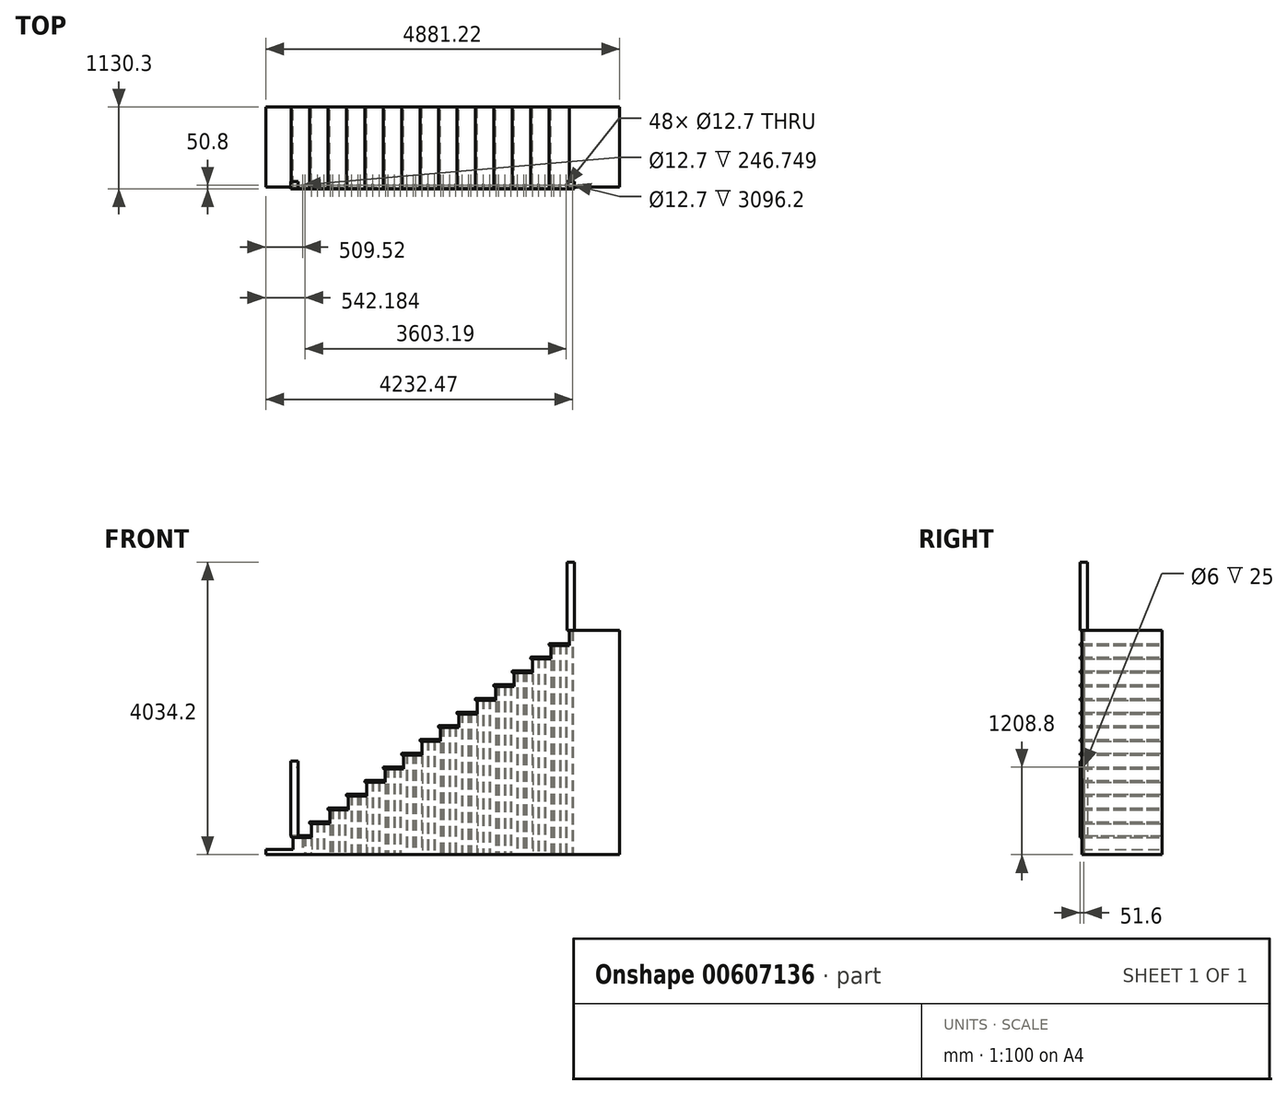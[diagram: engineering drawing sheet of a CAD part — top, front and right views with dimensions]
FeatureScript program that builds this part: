
annotation { "Feature Type Name" : "Feature", "Feature Type Description" : "" }
export const myFeature = defineFeature(function(context is Context, id is Id, definition is map)
    precondition{}
    {
        {
            var Q0;
            Q0=qCreatedBy(makeId("Front.planeOp"),FACE);
            var sketch = newSketch(context, id + "F0", { "sketchPlane" : qUnion([Q0])});
            skLineSegment(sketch, "E0.bottom", {"start": v(9.53, 0) * mm, "end": v(279.4, 0) * mm});
            skLineSegment(sketch, "E0.top", {"start": v(9.53, 25.4) * mm, "end": v(279.4, 25.4) * mm});
            skLineSegment(sketch, "E0.left", {"start": v(0, 9.52) * mm, "end": v(0, 15.88) * mm});
            skLineSegment(sketch, "E0.right", {"start": v(279.4, 0) * mm, "end": v(279.4, 25.4) * mm});
            skPoint(sketch, "E1.visualSharp", {"position": v(0, 25.4) * mm});
            skArc(sketch, "E1.filletArc", {"start": v(9.53, 25.4) * mm, "mid": v(2.79, 22.61) * mm, "end": v(0, 15.87) * mm});
            skPoint(sketch, "E2.visualSharp", {"position": v(0, 0) * mm});
            skArc(sketch, "E2.filletArc", {"start": v(0, 9.52) * mm, "mid": v(2.79, 2.79) * mm, "end": v(9.53, 0) * mm});
            skLineSegment(sketch, "E3.1.0.0", {"start": v(263.53, 189.1) * mm, "end": v(533.4, 189.1) * mm});
            skLineSegment(sketch, "E3.1.0.1", {"start": v(263.53, 214.5) * mm, "end": v(533.4, 214.5) * mm});
            skLineSegment(sketch, "E3.1.0.2", {"start": v(533.4, 189.1) * mm, "end": v(533.4, 214.5) * mm});
            skArc(sketch, "E3.1.0.3", {"start": v(263.53, 214.5) * mm, "mid": v(256.79, 211.71) * mm, "end": v(254, 204.98) * mm});
            skLineSegment(sketch, "E3.1.0.4", {"start": v(254, 198.63) * mm, "end": v(254, 204.98) * mm});
            skArc(sketch, "E3.1.0.5", {"start": v(254, 198.63) * mm, "mid": v(256.79, 191.89) * mm, "end": v(263.53, 189.1) * mm});
            skLineSegment(sketch, "E3.2.0.0", {"start": v(517.52, 378.2) * mm, "end": v(787.4, 378.2) * mm});
            skLineSegment(sketch, "E3.2.0.1", {"start": v(517.52, 403.6) * mm, "end": v(787.4, 403.6) * mm});
            skLineSegment(sketch, "E3.2.0.2", {"start": v(787.4, 378.2) * mm, "end": v(787.4, 403.6) * mm});
            skArc(sketch, "E3.2.0.3", {"start": v(517.52, 403.6) * mm, "mid": v(510.79, 400.81) * mm, "end": v(508, 394.07) * mm});
            skLineSegment(sketch, "E3.2.0.4", {"start": v(508, 387.73) * mm, "end": v(508, 394.07) * mm});
            skArc(sketch, "E3.2.0.5", {"start": v(508, 387.73) * mm, "mid": v(510.79, 380.99) * mm, "end": v(517.52, 378.2) * mm});
            skLineSegment(sketch, "E3.direction1", {"start": v(9.53, 0) * mm, "end": v(263.53, 189.1) * mm, "construction": true});
            skLineSegment(sketch, "E4.0.3.0", {"start": v(771.52, 567.3) * mm, "end": v(1041.4, 567.3) * mm});
            skLineSegment(sketch, "E4.3.3.0", {"start": v(771.52, 592.7) * mm, "end": v(1041.4, 592.7) * mm});
            skLineSegment(sketch, "E4.6.3.0", {"start": v(1041.4, 567.3) * mm, "end": v(1041.4, 592.7) * mm});
            skArc(sketch, "E4.9.3.0", {"start": v(771.52, 592.7) * mm, "mid": v(764.79, 589.91) * mm, "end": v(762, 583.18) * mm});
            skLineSegment(sketch, "E4.13.3.0", {"start": v(762, 576.82) * mm, "end": v(762, 583.18) * mm});
            skArc(sketch, "E4.16.3.0", {"start": v(762, 576.82) * mm, "mid": v(764.79, 570.09) * mm, "end": v(771.52, 567.3) * mm});
            skLineSegment(sketch, "E4.0.4.0", {"start": v(1025.53, 756.4) * mm, "end": v(1295.4, 756.4) * mm});
            skLineSegment(sketch, "E4.3.4.0", {"start": v(1025.53, 781.8) * mm, "end": v(1295.4, 781.8) * mm});
            skLineSegment(sketch, "E4.6.4.0", {"start": v(1295.4, 756.4) * mm, "end": v(1295.4, 781.8) * mm});
            skArc(sketch, "E4.9.4.0", {"start": v(1025.53, 781.8) * mm, "mid": v(1018.79, 779.01) * mm, "end": v(1016, 772.28) * mm});
            skLineSegment(sketch, "E4.13.4.0", {"start": v(1016, 765.93) * mm, "end": v(1016, 772.28) * mm});
            skArc(sketch, "E4.16.4.0", {"start": v(1016, 765.93) * mm, "mid": v(1018.79, 759.19) * mm, "end": v(1025.53, 756.4) * mm});
            skLineSegment(sketch, "E4.0.5.0", {"start": v(1279.53, 945.5) * mm, "end": v(1549.4, 945.5) * mm});
            skLineSegment(sketch, "E4.3.5.0", {"start": v(1279.53, 970.9) * mm, "end": v(1549.4, 970.9) * mm});
            skLineSegment(sketch, "E4.6.5.0", {"start": v(1549.4, 945.5) * mm, "end": v(1549.4, 970.9) * mm});
            skArc(sketch, "E4.9.5.0", {"start": v(1279.53, 970.9) * mm, "mid": v(1272.79, 968.11) * mm, "end": v(1270, 961.38) * mm});
            skLineSegment(sketch, "E4.13.5.0", {"start": v(1270, 955.02) * mm, "end": v(1270, 961.38) * mm});
            skArc(sketch, "E4.16.5.0", {"start": v(1270, 955.02) * mm, "mid": v(1272.79, 948.29) * mm, "end": v(1279.53, 945.5) * mm});
            skLineSegment(sketch, "E4.0.6.0", {"start": v(1533.53, 1134.6) * mm, "end": v(1803.4, 1134.6) * mm});
            skLineSegment(sketch, "E4.3.6.0", {"start": v(1533.53, 1160) * mm, "end": v(1803.4, 1160) * mm});
            skLineSegment(sketch, "E4.6.6.0", {"start": v(1803.4, 1134.6) * mm, "end": v(1803.4, 1160) * mm});
            skArc(sketch, "E4.9.6.0", {"start": v(1533.53, 1160) * mm, "mid": v(1526.79, 1157.21) * mm, "end": v(1524, 1150.48) * mm});
            skLineSegment(sketch, "E4.13.6.0", {"start": v(1524, 1144.12) * mm, "end": v(1524, 1150.48) * mm});
            skArc(sketch, "E4.16.6.0", {"start": v(1524, 1144.12) * mm, "mid": v(1526.79, 1137.39) * mm, "end": v(1533.53, 1134.6) * mm});
            skLineSegment(sketch, "E4.0.7.0", {"start": v(1787.53, 1323.7) * mm, "end": v(2057.4, 1323.7) * mm});
            skLineSegment(sketch, "E4.3.7.0", {"start": v(1787.53, 1349.1) * mm, "end": v(2057.4, 1349.1) * mm});
            skLineSegment(sketch, "E4.6.7.0", {"start": v(2057.4, 1323.7) * mm, "end": v(2057.4, 1349.1) * mm});
            skArc(sketch, "E4.9.7.0", {"start": v(1787.53, 1349.1) * mm, "mid": v(1780.79, 1346.31) * mm, "end": v(1778, 1339.58) * mm});
            skLineSegment(sketch, "E4.13.7.0", {"start": v(1778, 1333.23) * mm, "end": v(1778, 1339.58) * mm});
            skArc(sketch, "E4.16.7.0", {"start": v(1778, 1333.23) * mm, "mid": v(1780.79, 1326.49) * mm, "end": v(1787.53, 1323.7) * mm});
            skLineSegment(sketch, "E4.0.8.0", {"start": v(2041.53, 1512.8) * mm, "end": v(2311.4, 1512.8) * mm});
            skLineSegment(sketch, "E4.3.8.0", {"start": v(2041.53, 1538.2) * mm, "end": v(2311.4, 1538.2) * mm});
            skLineSegment(sketch, "E4.6.8.0", {"start": v(2311.4, 1512.8) * mm, "end": v(2311.4, 1538.2) * mm});
            skArc(sketch, "E4.9.8.0", {"start": v(2041.53, 1538.2) * mm, "mid": v(2034.79, 1535.41) * mm, "end": v(2032, 1528.67) * mm});
            skLineSegment(sketch, "E4.13.8.0", {"start": v(2032, 1522.33) * mm, "end": v(2032, 1528.67) * mm});
            skArc(sketch, "E4.16.8.0", {"start": v(2032, 1522.33) * mm, "mid": v(2034.79, 1515.59) * mm, "end": v(2041.53, 1512.8) * mm});
            skLineSegment(sketch, "E4.0.9.0", {"start": v(2295.53, 1701.9) * mm, "end": v(2565.4, 1701.9) * mm});
            skLineSegment(sketch, "E4.3.9.0", {"start": v(2295.53, 1727.3) * mm, "end": v(2565.4, 1727.3) * mm});
            skLineSegment(sketch, "E4.6.9.0", {"start": v(2565.4, 1701.9) * mm, "end": v(2565.4, 1727.3) * mm});
            skArc(sketch, "E4.9.9.0", {"start": v(2295.53, 1727.3) * mm, "mid": v(2288.79, 1724.51) * mm, "end": v(2286, 1717.77) * mm});
            skLineSegment(sketch, "E4.13.9.0", {"start": v(2286, 1711.43) * mm, "end": v(2286, 1717.77) * mm});
            skArc(sketch, "E4.16.9.0", {"start": v(2286, 1711.43) * mm, "mid": v(2288.79, 1704.69) * mm, "end": v(2295.53, 1701.9) * mm});
            skLineSegment(sketch, "E4.0.10.0", {"start": v(2549.53, 1891) * mm, "end": v(2819.4, 1891) * mm});
            skLineSegment(sketch, "E4.3.10.0", {"start": v(2549.53, 1916.4) * mm, "end": v(2819.4, 1916.4) * mm});
            skLineSegment(sketch, "E4.6.10.0", {"start": v(2819.4, 1891) * mm, "end": v(2819.4, 1916.4) * mm});
            skArc(sketch, "E4.9.10.0", {"start": v(2549.53, 1916.4) * mm, "mid": v(2542.79, 1913.61) * mm, "end": v(2540, 1906.87) * mm});
            skLineSegment(sketch, "E4.13.10.0", {"start": v(2540, 1900.53) * mm, "end": v(2540, 1906.87) * mm});
            skArc(sketch, "E4.16.10.0", {"start": v(2540, 1900.53) * mm, "mid": v(2542.79, 1893.79) * mm, "end": v(2549.53, 1891) * mm});
            skLineSegment(sketch, "E4.0.11.0", {"start": v(2803.53, 2080.1) * mm, "end": v(3073.4, 2080.1) * mm});
            skLineSegment(sketch, "E4.3.11.0", {"start": v(2803.53, 2105.5) * mm, "end": v(3073.4, 2105.5) * mm});
            skLineSegment(sketch, "E4.6.11.0", {"start": v(3073.4, 2080.1) * mm, "end": v(3073.4, 2105.5) * mm});
            skArc(sketch, "E4.9.11.0", {"start": v(2803.53, 2105.5) * mm, "mid": v(2796.79, 2102.71) * mm, "end": v(2794, 2095.98) * mm});
            skLineSegment(sketch, "E4.13.11.0", {"start": v(2794, 2089.62) * mm, "end": v(2794, 2095.98) * mm});
            skArc(sketch, "E4.16.11.0", {"start": v(2794, 2089.62) * mm, "mid": v(2796.79, 2082.89) * mm, "end": v(2803.53, 2080.1) * mm});
            skLineSegment(sketch, "E4.0.12.0", {"start": v(3057.53, 2269.2) * mm, "end": v(3327.4, 2269.2) * mm});
            skLineSegment(sketch, "E4.3.12.0", {"start": v(3057.53, 2294.6) * mm, "end": v(3327.4, 2294.6) * mm});
            skLineSegment(sketch, "E4.6.12.0", {"start": v(3327.4, 2269.2) * mm, "end": v(3327.4, 2294.6) * mm});
            skArc(sketch, "E4.9.12.0", {"start": v(3057.53, 2294.6) * mm, "mid": v(3050.79, 2291.81) * mm, "end": v(3048, 2285.08) * mm});
            skLineSegment(sketch, "E4.13.12.0", {"start": v(3048, 2278.72) * mm, "end": v(3048, 2285.08) * mm});
            skArc(sketch, "E4.16.12.0", {"start": v(3048, 2278.72) * mm, "mid": v(3050.79, 2271.99) * mm, "end": v(3057.53, 2269.2) * mm});
            skLineSegment(sketch, "E4.0.13.0", {"start": v(3311.53, 2458.3) * mm, "end": v(3581.4, 2458.3) * mm});
            skLineSegment(sketch, "E4.3.13.0", {"start": v(3311.53, 2483.7) * mm, "end": v(3581.4, 2483.7) * mm});
            skLineSegment(sketch, "E4.6.13.0", {"start": v(3581.4, 2458.3) * mm, "end": v(3581.4, 2483.7) * mm});
            skArc(sketch, "E4.9.13.0", {"start": v(3311.53, 2483.7) * mm, "mid": v(3304.79, 2480.91) * mm, "end": v(3302, 2474.18) * mm});
            skLineSegment(sketch, "E4.13.13.0", {"start": v(3302, 2467.83) * mm, "end": v(3302, 2474.18) * mm});
            skArc(sketch, "E4.16.13.0", {"start": v(3302, 2467.83) * mm, "mid": v(3304.79, 2461.09) * mm, "end": v(3311.53, 2458.3) * mm});
            skLineSegment(sketch, "E4.0.14.0", {"start": v(3565.53, 2647.4) * mm, "end": v(3835.4, 2647.4) * mm});
            skLineSegment(sketch, "E4.3.14.0", {"start": v(3565.53, 2672.8) * mm, "end": v(3835.4, 2672.8) * mm});
            skLineSegment(sketch, "E4.6.14.0", {"start": v(3835.4, 2647.4) * mm, "end": v(3835.4, 2672.8) * mm});
            skArc(sketch, "E4.9.14.0", {"start": v(3565.53, 2672.8) * mm, "mid": v(3558.79, 2670.01) * mm, "end": v(3556, 2663.28) * mm});
            skLineSegment(sketch, "E4.13.14.0", {"start": v(3556, 2656.93) * mm, "end": v(3556, 2663.28) * mm});
            skArc(sketch, "E4.16.14.0", {"start": v(3556, 2656.93) * mm, "mid": v(3558.79, 2650.19) * mm, "end": v(3565.53, 2647.4) * mm});
            skPoint(sketch, "E5.start.orphan", {"position": v(279.4, 25.4) * mm});
            skLineSegment(sketch, "E6", {"start": v(25.4, 0) * mm, "end": v(25.4, -170) * mm});
            skLineSegment(sketch, "E7", {"start": v(25.4, -170) * mm, "end": v(-349.5, -170) * mm});
            skLineSegment(sketch, "E8", {"start": v(-349.5, -170) * mm, "end": v(-349.5, -240.4) * mm});
            skLineSegment(sketch, "E9", {"start": v(-349.5, -240.4) * mm, "end": v(4531.72, -240.4) * mm});
            skLineSegment(sketch, "E10", {"start": v(4531.72, -240.4) * mm, "end": v(4531.72, 2855.8) * mm});
            skLineSegment(sketch, "E11", {"start": v(4531.72, 2855.8) * mm, "end": v(3835.4, 2855.8) * mm});
            skLineSegment(sketch, "E12", {"start": v(3835.4, 2855.8) * mm, "end": v(3835.4, 2647.4) * mm});
            skLineSegment(sketch, "E13", {"start": v(3581.4, 2483.7) * mm, "end": v(3581.4, 2647.4) * mm});
            skLineSegment(sketch, "E14", {"start": v(3327.4, 2294.6) * mm, "end": v(3327.4, 2458.3) * mm});
            skLineSegment(sketch, "E15", {"start": v(3073.4, 2105.5) * mm, "end": v(3073.4, 2269.2) * mm});
            skLineSegment(sketch, "E16", {"start": v(2819.4, 1916.4) * mm, "end": v(2819.4, 2080.1) * mm});
            skLineSegment(sketch, "E17", {"start": v(2565.4, 1727.3) * mm, "end": v(2565.4, 1891) * mm});
            skLineSegment(sketch, "E18", {"start": v(2311.4, 1538.2) * mm, "end": v(2311.4, 1701.9) * mm});
            skLineSegment(sketch, "E19", {"start": v(2057.4, 1349.1) * mm, "end": v(2057.4, 1512.8) * mm});
            skLineSegment(sketch, "E20", {"start": v(1803.4, 1160) * mm, "end": v(1803.4, 1323.7) * mm});
            skLineSegment(sketch, "E21", {"start": v(1549.4, 970.9) * mm, "end": v(1549.4, 1134.6) * mm});
            skLineSegment(sketch, "E22", {"start": v(1295.4, 781.8) * mm, "end": v(1295.4, 945.5) * mm});
            skLineSegment(sketch, "E23", {"start": v(1041.4, 592.7) * mm, "end": v(1041.4, 756.4) * mm});
            skLineSegment(sketch, "E24", {"start": v(787.4, 403.6) * mm, "end": v(787.4, 567.3) * mm});
            skLineSegment(sketch, "E25", {"start": v(533.4, 214.5) * mm, "end": v(533.4, 378.2) * mm});
            skLineSegment(sketch, "E26", {"start": v(279.4, 25.4) * mm, "end": v(279.4, 189.1) * mm});
            skLineSegment(sketch, "E27", {"start": v(92.07, 542.4) * mm, "end": v(92.08, -396.52) * mm, "construction": true});
            skSolve(sketch);
        }
        {
            var Q0;
            Q0=qSketchRegion(id+"F0",true);
            extrude(context, id + "F1", {"entities" : qUnion([Q0]), "depth" : 1104.9 * mm, "offsetDistance" : 25.4 * mm});
        }
        {
            var Q0;
            Q0=makeQuery(id+"F1.opExtrude","CAP_FACE",FACE,{"disambiguationData":[OSD([sQuery(id+"F0.wireOp",EDGE,"E0.bottom"),sQuery(id+"F0.wireOp",EDGE,"E0.top"),sQuery(id+"F0.wireOp",EDGE,"E0.left"),sQuery(id+"F0.wireOp",EDGE,"E1.filletArc"),sQuery(id+"F0.wireOp",EDGE,"E2.filletArc"),sQuery(id+"F0.wireOp",EDGE,"E3.1.0.0"),sQuery(id+"F0.wireOp",EDGE,"E3.1.0.1"),sQuery(id+"F0.wireOp",EDGE,"E3.1.0.3"),sQuery(id+"F0.wireOp",EDGE,"E3.1.0.4"),sQuery(id+"F0.wireOp",EDGE,"E3.1.0.5"),sQuery(id+"F0.wireOp",EDGE,"E3.2.0.0"),sQuery(id+"F0.wireOp",EDGE,"E3.2.0.1"),sQuery(id+"F0.wireOp",EDGE,"E3.2.0.3"),sQuery(id+"F0.wireOp",EDGE,"E3.2.0.4"),sQuery(id+"F0.wireOp",EDGE,"E3.2.0.5"),sQuery(id+"F0.wireOp",EDGE,"E4.0.3.0"),sQuery(id+"F0.wireOp",EDGE,"E4.3.3.0"),sQuery(id+"F0.wireOp",EDGE,"E4.9.3.0"),sQuery(id+"F0.wireOp",EDGE,"E4.13.3.0"),sQuery(id+"F0.wireOp",EDGE,"E4.16.3.0"),sQuery(id+"F0.wireOp",EDGE,"E4.0.4.0"),sQuery(id+"F0.wireOp",EDGE,"E4.3.4.0"),sQuery(id+"F0.wireOp",EDGE,"E4.9.4.0"),sQuery(id+"F0.wireOp",EDGE,"E4.13.4.0"),sQuery(id+"F0.wireOp",EDGE,"E4.16.4.0"),sQuery(id+"F0.wireOp",EDGE,"E4.0.5.0"),sQuery(id+"F0.wireOp",EDGE,"E4.3.5.0"),sQuery(id+"F0.wireOp",EDGE,"E4.9.5.0"),sQuery(id+"F0.wireOp",EDGE,"E4.13.5.0"),sQuery(id+"F0.wireOp",EDGE,"E4.16.5.0"),sQuery(id+"F0.wireOp",EDGE,"E4.0.6.0"),sQuery(id+"F0.wireOp",EDGE,"E4.3.6.0"),sQuery(id+"F0.wireOp",EDGE,"E4.9.6.0"),sQuery(id+"F0.wireOp",EDGE,"E4.13.6.0"),sQuery(id+"F0.wireOp",EDGE,"E4.16.6.0"),sQuery(id+"F0.wireOp",EDGE,"E4.0.7.0"),sQuery(id+"F0.wireOp",EDGE,"E4.3.7.0"),sQuery(id+"F0.wireOp",EDGE,"E4.9.7.0"),sQuery(id+"F0.wireOp",EDGE,"E4.13.7.0"),sQuery(id+"F0.wireOp",EDGE,"E4.16.7.0"),sQuery(id+"F0.wireOp",EDGE,"E4.0.8.0"),sQuery(id+"F0.wireOp",EDGE,"E4.3.8.0"),sQuery(id+"F0.wireOp",EDGE,"E4.9.8.0"),sQuery(id+"F0.wireOp",EDGE,"E4.13.8.0"),sQuery(id+"F0.wireOp",EDGE,"E4.16.8.0"),sQuery(id+"F0.wireOp",EDGE,"E4.0.9.0"),sQuery(id+"F0.wireOp",EDGE,"E4.3.9.0"),sQuery(id+"F0.wireOp",EDGE,"E4.9.9.0"),sQuery(id+"F0.wireOp",EDGE,"E4.13.9.0"),sQuery(id+"F0.wireOp",EDGE,"E4.16.9.0"),sQuery(id+"F0.wireOp",EDGE,"E4.0.10.0"),sQuery(id+"F0.wireOp",EDGE,"E4.3.10.0"),sQuery(id+"F0.wireOp",EDGE,"E4.9.10.0"),sQuery(id+"F0.wireOp",EDGE,"E4.13.10.0"),sQuery(id+"F0.wireOp",EDGE,"E4.16.10.0"),sQuery(id+"F0.wireOp",EDGE,"E4.0.11.0"),sQuery(id+"F0.wireOp",EDGE,"E4.3.11.0"),sQuery(id+"F0.wireOp",EDGE,"E4.9.11.0"),sQuery(id+"F0.wireOp",EDGE,"E4.13.11.0"),sQuery(id+"F0.wireOp",EDGE,"E4.16.11.0"),sQuery(id+"F0.wireOp",EDGE,"E4.0.12.0"),sQuery(id+"F0.wireOp",EDGE,"E4.3.12.0"),sQuery(id+"F0.wireOp",EDGE,"E4.9.12.0"),sQuery(id+"F0.wireOp",EDGE,"E4.13.12.0"),sQuery(id+"F0.wireOp",EDGE,"E4.16.12.0"),sQuery(id+"F0.wireOp",EDGE,"E4.0.13.0"),sQuery(id+"F0.wireOp",EDGE,"E4.3.13.0"),sQuery(id+"F0.wireOp",EDGE,"E4.9.13.0"),sQuery(id+"F0.wireOp",EDGE,"E4.13.13.0"),sQuery(id+"F0.wireOp",EDGE,"E4.16.13.0"),sQuery(id+"F0.wireOp",EDGE,"E4.0.14.0"),sQuery(id+"F0.wireOp",EDGE,"E4.3.14.0"),sQuery(id+"F0.wireOp",EDGE,"E4.9.14.0"),sQuery(id+"F0.wireOp",EDGE,"E4.13.14.0"),sQuery(id+"F0.wireOp",EDGE,"E4.16.14.0"),sQuery(id+"F0.wireOp",EDGE,"E6"),sQuery(id+"F0.wireOp",EDGE,"E7"),sQuery(id+"F0.wireOp",EDGE,"E8"),sQuery(id+"F0.wireOp",EDGE,"E9"),sQuery(id+"F0.wireOp",EDGE,"E10"),sQuery(id+"F0.wireOp",EDGE,"E11"),sQuery(id+"F0.wireOp",EDGE,"E12"),sQuery(id+"F0.wireOp",EDGE,"E13"),sQuery(id+"F0.wireOp",EDGE,"E14"),sQuery(id+"F0.wireOp",EDGE,"E15"),sQuery(id+"F0.wireOp",EDGE,"E16"),sQuery(id+"F0.wireOp",EDGE,"E17"),sQuery(id+"F0.wireOp",EDGE,"E18"),sQuery(id+"F0.wireOp",EDGE,"E19"),sQuery(id+"F0.wireOp",EDGE,"E20"),sQuery(id+"F0.wireOp",EDGE,"E21"),sQuery(id+"F0.wireOp",EDGE,"E22"),sQuery(id+"F0.wireOp",EDGE,"E23"),sQuery(id+"F0.wireOp",EDGE,"E24"),sQuery(id+"F0.wireOp",EDGE,"E25"),sQuery(id+"F0.wireOp",EDGE,"E26")])],"isStart":false});
            var sketch = newSketch(context, id + "F2", { "sketchPlane" : qUnion([Q0])});
            skLineSegment(sketch, "E28.0", {"start": v(9.53, 0) * mm, "end": v(25.4, 0) * mm});
            skArc(sketch, "E28.1", {"start": v(0, 9.52) * mm, "mid": v(2.79, 2.79) * mm, "end": v(9.53, 0) * mm});
            skLineSegment(sketch, "E28.2", {"start": v(0, 9.52) * mm, "end": v(0, 15.88) * mm});
            skArc(sketch, "E28.3", {"start": v(9.53, 25.4) * mm, "mid": v(2.79, 22.61) * mm, "end": v(0, 15.88) * mm});
            skLineSegment(sketch, "E28.4", {"start": v(9.53, 25.4) * mm, "end": v(279.4, 25.4) * mm});
            skPoint(sketch, "E28.5", {"position": v(17.46, 0) * mm});
            skPoint(sketch, "E28.6", {"position": v(2.79, 2.79) * mm});
            skLineSegment(sketch, "E29", {"start": v(279.4, 25.4) * mm, "end": v(279.4, 0) * mm});
            skLineSegment(sketch, "E30", {"start": v(25.4, 0) * mm, "end": v(279.4, 0) * mm});
            skLineSegment(sketch, "E31.1.0.0", {"start": v(263.52, 214.5) * mm, "end": v(533.4, 214.5) * mm});
            skLineSegment(sketch, "E31.1.0.1", {"start": v(279.4, 189.1) * mm, "end": v(533.4, 189.1) * mm});
            skPoint(sketch, "E31.1.0.2", {"position": v(271.46, 189.1) * mm});
            skPoint(sketch, "E31.1.0.3", {"position": v(256.79, 191.89) * mm});
            skLineSegment(sketch, "E31.1.0.4", {"start": v(533.4, 214.5) * mm, "end": v(533.4, 189.1) * mm});
            skArc(sketch, "E31.1.0.5", {"start": v(254, 198.63) * mm, "mid": v(256.79, 191.89) * mm, "end": v(263.52, 189.1) * mm});
            skLineSegment(sketch, "E31.1.0.6", {"start": v(263.52, 189.1) * mm, "end": v(279.4, 189.1) * mm});
            skLineSegment(sketch, "E31.1.0.7", {"start": v(254, 198.63) * mm, "end": v(254, 204.98) * mm});
            skArc(sketch, "E31.1.0.8", {"start": v(263.52, 214.5) * mm, "mid": v(256.79, 211.71) * mm, "end": v(254, 204.98) * mm});
            skLineSegment(sketch, "E31.2.0.0", {"start": v(517.52, 403.6) * mm, "end": v(787.4, 403.6) * mm});
            skLineSegment(sketch, "E31.2.0.1", {"start": v(533.4, 378.2) * mm, "end": v(787.4, 378.2) * mm});
            skPoint(sketch, "E31.2.0.2", {"position": v(525.46, 378.2) * mm});
            skPoint(sketch, "E31.2.0.3", {"position": v(510.79, 380.99) * mm});
            skLineSegment(sketch, "E31.2.0.4", {"start": v(787.4, 403.6) * mm, "end": v(787.4, 378.2) * mm});
            skArc(sketch, "E31.2.0.5", {"start": v(508, 387.73) * mm, "mid": v(510.79, 380.99) * mm, "end": v(517.52, 378.2) * mm});
            skLineSegment(sketch, "E31.2.0.6", {"start": v(517.52, 378.2) * mm, "end": v(533.4, 378.2) * mm});
            skLineSegment(sketch, "E31.2.0.7", {"start": v(508, 387.73) * mm, "end": v(508, 394.08) * mm});
            skArc(sketch, "E31.2.0.8", {"start": v(517.52, 403.6) * mm, "mid": v(510.79, 400.81) * mm, "end": v(508, 394.08) * mm});
            skLineSegment(sketch, "E31.direction1", {"start": v(2.79, 2.79) * mm, "end": v(256.79, 191.89) * mm, "construction": true});
            skLineSegment(sketch, "E32.0.3.0", {"start": v(771.52, 592.7) * mm, "end": v(1041.4, 592.7) * mm});
            skLineSegment(sketch, "E32.3.3.0", {"start": v(787.4, 567.3) * mm, "end": v(1041.4, 567.3) * mm});
            skPoint(sketch, "E32.6.3.0", {"position": v(779.46, 567.3) * mm});
            skPoint(sketch, "E32.7.3.0", {"position": v(764.79, 570.09) * mm});
            skLineSegment(sketch, "E32.8.3.0", {"start": v(1041.4, 592.7) * mm, "end": v(1041.4, 567.3) * mm});
            skArc(sketch, "E32.11.3.0", {"start": v(762, 576.83) * mm, "mid": v(764.79, 570.09) * mm, "end": v(771.52, 567.3) * mm});
            skLineSegment(sketch, "E32.15.3.0", {"start": v(771.52, 567.3) * mm, "end": v(787.4, 567.3) * mm});
            skLineSegment(sketch, "E32.18.3.0", {"start": v(762, 576.83) * mm, "end": v(762, 583.17) * mm});
            skArc(sketch, "E32.21.3.0", {"start": v(771.52, 592.7) * mm, "mid": v(764.79, 589.91) * mm, "end": v(762, 583.17) * mm});
            skLineSegment(sketch, "E32.0.4.0", {"start": v(1025.52, 781.8) * mm, "end": v(1295.4, 781.8) * mm});
            skLineSegment(sketch, "E32.3.4.0", {"start": v(1041.4, 756.4) * mm, "end": v(1295.4, 756.4) * mm});
            skPoint(sketch, "E32.6.4.0", {"position": v(1033.46, 756.4) * mm});
            skPoint(sketch, "E32.7.4.0", {"position": v(1018.79, 759.19) * mm});
            skLineSegment(sketch, "E32.8.4.0", {"start": v(1295.4, 781.8) * mm, "end": v(1295.4, 756.4) * mm});
            skArc(sketch, "E32.11.4.0", {"start": v(1016, 765.93) * mm, "mid": v(1018.79, 759.19) * mm, "end": v(1025.52, 756.4) * mm});
            skLineSegment(sketch, "E32.15.4.0", {"start": v(1025.52, 756.4) * mm, "end": v(1041.4, 756.4) * mm});
            skLineSegment(sketch, "E32.18.4.0", {"start": v(1016, 765.93) * mm, "end": v(1016, 772.28) * mm});
            skArc(sketch, "E32.21.4.0", {"start": v(1025.52, 781.8) * mm, "mid": v(1018.79, 779.01) * mm, "end": v(1016, 772.28) * mm});
            skLineSegment(sketch, "E32.0.5.0", {"start": v(1279.52, 970.9) * mm, "end": v(1549.4, 970.9) * mm});
            skLineSegment(sketch, "E32.3.5.0", {"start": v(1295.4, 945.5) * mm, "end": v(1549.4, 945.5) * mm});
            skPoint(sketch, "E32.6.5.0", {"position": v(1287.46, 945.5) * mm});
            skPoint(sketch, "E32.7.5.0", {"position": v(1272.79, 948.29) * mm});
            skLineSegment(sketch, "E32.8.5.0", {"start": v(1549.4, 970.9) * mm, "end": v(1549.4, 945.5) * mm});
            skArc(sketch, "E32.11.5.0", {"start": v(1270, 955.03) * mm, "mid": v(1272.79, 948.29) * mm, "end": v(1279.52, 945.5) * mm});
            skLineSegment(sketch, "E32.15.5.0", {"start": v(1279.52, 945.5) * mm, "end": v(1295.4, 945.5) * mm});
            skLineSegment(sketch, "E32.18.5.0", {"start": v(1270, 955.03) * mm, "end": v(1270, 961.38) * mm});
            skArc(sketch, "E32.21.5.0", {"start": v(1279.52, 970.9) * mm, "mid": v(1272.79, 968.11) * mm, "end": v(1270, 961.38) * mm});
            skLineSegment(sketch, "E32.0.6.0", {"start": v(1533.52, 1160) * mm, "end": v(1803.4, 1160) * mm});
            skLineSegment(sketch, "E32.3.6.0", {"start": v(1549.4, 1134.6) * mm, "end": v(1803.4, 1134.6) * mm});
            skPoint(sketch, "E32.6.6.0", {"position": v(1541.46, 1134.6) * mm});
            skPoint(sketch, "E32.7.6.0", {"position": v(1526.79, 1137.39) * mm});
            skLineSegment(sketch, "E32.8.6.0", {"start": v(1803.4, 1160) * mm, "end": v(1803.4, 1134.6) * mm});
            skArc(sketch, "E32.11.6.0", {"start": v(1524, 1144.12) * mm, "mid": v(1526.79, 1137.39) * mm, "end": v(1533.52, 1134.6) * mm});
            skLineSegment(sketch, "E32.15.6.0", {"start": v(1533.52, 1134.6) * mm, "end": v(1549.4, 1134.6) * mm});
            skLineSegment(sketch, "E32.18.6.0", {"start": v(1524, 1144.12) * mm, "end": v(1524, 1150.48) * mm});
            skArc(sketch, "E32.21.6.0", {"start": v(1533.52, 1160) * mm, "mid": v(1526.79, 1157.21) * mm, "end": v(1524, 1150.48) * mm});
            skLineSegment(sketch, "E32.0.7.0", {"start": v(1787.52, 1349.1) * mm, "end": v(2057.4, 1349.1) * mm});
            skLineSegment(sketch, "E32.3.7.0", {"start": v(1803.4, 1323.7) * mm, "end": v(2057.4, 1323.7) * mm});
            skPoint(sketch, "E32.6.7.0", {"position": v(1795.46, 1323.7) * mm});
            skPoint(sketch, "E32.7.7.0", {"position": v(1780.79, 1326.49) * mm});
            skLineSegment(sketch, "E32.8.7.0", {"start": v(2057.4, 1349.1) * mm, "end": v(2057.4, 1323.7) * mm});
            skArc(sketch, "E32.11.7.0", {"start": v(1778, 1333.23) * mm, "mid": v(1780.79, 1326.49) * mm, "end": v(1787.52, 1323.7) * mm});
            skLineSegment(sketch, "E32.15.7.0", {"start": v(1787.52, 1323.7) * mm, "end": v(1803.4, 1323.7) * mm});
            skLineSegment(sketch, "E32.18.7.0", {"start": v(1778, 1333.23) * mm, "end": v(1778, 1339.58) * mm});
            skArc(sketch, "E32.21.7.0", {"start": v(1787.52, 1349.1) * mm, "mid": v(1780.79, 1346.31) * mm, "end": v(1778, 1339.58) * mm});
            skLineSegment(sketch, "E32.0.8.0", {"start": v(2041.52, 1538.2) * mm, "end": v(2311.4, 1538.2) * mm});
            skLineSegment(sketch, "E32.3.8.0", {"start": v(2057.4, 1512.8) * mm, "end": v(2311.4, 1512.8) * mm});
            skPoint(sketch, "E32.6.8.0", {"position": v(2049.46, 1512.8) * mm});
            skPoint(sketch, "E32.7.8.0", {"position": v(2034.79, 1515.59) * mm});
            skLineSegment(sketch, "E32.8.8.0", {"start": v(2311.4, 1538.2) * mm, "end": v(2311.4, 1512.8) * mm});
            skArc(sketch, "E32.11.8.0", {"start": v(2032, 1522.33) * mm, "mid": v(2034.79, 1515.59) * mm, "end": v(2041.52, 1512.8) * mm});
            skLineSegment(sketch, "E32.15.8.0", {"start": v(2041.52, 1512.8) * mm, "end": v(2057.4, 1512.8) * mm});
            skLineSegment(sketch, "E32.18.8.0", {"start": v(2032, 1522.33) * mm, "end": v(2032, 1528.68) * mm});
            skArc(sketch, "E32.21.8.0", {"start": v(2041.52, 1538.2) * mm, "mid": v(2034.79, 1535.41) * mm, "end": v(2032, 1528.68) * mm});
            skLineSegment(sketch, "E32.0.9.0", {"start": v(2295.52, 1727.3) * mm, "end": v(2565.4, 1727.3) * mm});
            skLineSegment(sketch, "E32.3.9.0", {"start": v(2311.4, 1701.9) * mm, "end": v(2565.4, 1701.9) * mm});
            skPoint(sketch, "E32.6.9.0", {"position": v(2303.46, 1701.9) * mm});
            skPoint(sketch, "E32.7.9.0", {"position": v(2288.79, 1704.69) * mm});
            skLineSegment(sketch, "E32.8.9.0", {"start": v(2565.4, 1727.3) * mm, "end": v(2565.4, 1701.9) * mm});
            skArc(sketch, "E32.11.9.0", {"start": v(2286, 1711.43) * mm, "mid": v(2288.79, 1704.69) * mm, "end": v(2295.52, 1701.9) * mm});
            skLineSegment(sketch, "E32.15.9.0", {"start": v(2295.52, 1701.9) * mm, "end": v(2311.4, 1701.9) * mm});
            skLineSegment(sketch, "E32.18.9.0", {"start": v(2286, 1711.43) * mm, "end": v(2286, 1717.78) * mm});
            skArc(sketch, "E32.21.9.0", {"start": v(2295.52, 1727.3) * mm, "mid": v(2288.79, 1724.51) * mm, "end": v(2286, 1717.78) * mm});
            skLineSegment(sketch, "E32.0.10.0", {"start": v(2549.52, 1916.4) * mm, "end": v(2819.4, 1916.4) * mm});
            skLineSegment(sketch, "E32.3.10.0", {"start": v(2565.4, 1891) * mm, "end": v(2819.4, 1891) * mm});
            skPoint(sketch, "E32.6.10.0", {"position": v(2557.46, 1891) * mm});
            skPoint(sketch, "E32.7.10.0", {"position": v(2542.79, 1893.79) * mm});
            skLineSegment(sketch, "E32.8.10.0", {"start": v(2819.4, 1916.4) * mm, "end": v(2819.4, 1891) * mm});
            skArc(sketch, "E32.11.10.0", {"start": v(2540, 1900.53) * mm, "mid": v(2542.79, 1893.79) * mm, "end": v(2549.52, 1891) * mm});
            skLineSegment(sketch, "E32.15.10.0", {"start": v(2549.52, 1891) * mm, "end": v(2565.4, 1891) * mm});
            skLineSegment(sketch, "E32.18.10.0", {"start": v(2540, 1900.53) * mm, "end": v(2540, 1906.88) * mm});
            skArc(sketch, "E32.21.10.0", {"start": v(2549.52, 1916.4) * mm, "mid": v(2542.79, 1913.61) * mm, "end": v(2540, 1906.88) * mm});
            skLineSegment(sketch, "E32.0.11.0", {"start": v(2803.52, 2105.5) * mm, "end": v(3073.4, 2105.5) * mm});
            skLineSegment(sketch, "E32.3.11.0", {"start": v(2819.4, 2080.1) * mm, "end": v(3073.4, 2080.1) * mm});
            skPoint(sketch, "E32.6.11.0", {"position": v(2811.46, 2080.1) * mm});
            skPoint(sketch, "E32.7.11.0", {"position": v(2796.79, 2082.89) * mm});
            skLineSegment(sketch, "E32.8.11.0", {"start": v(3073.4, 2105.5) * mm, "end": v(3073.4, 2080.1) * mm});
            skArc(sketch, "E32.11.11.0", {"start": v(2794, 2089.63) * mm, "mid": v(2796.79, 2082.89) * mm, "end": v(2803.52, 2080.1) * mm});
            skLineSegment(sketch, "E32.15.11.0", {"start": v(2803.52, 2080.1) * mm, "end": v(2819.4, 2080.1) * mm});
            skLineSegment(sketch, "E32.18.11.0", {"start": v(2794, 2089.63) * mm, "end": v(2794, 2095.98) * mm});
            skArc(sketch, "E32.21.11.0", {"start": v(2803.52, 2105.5) * mm, "mid": v(2796.79, 2102.71) * mm, "end": v(2794, 2095.98) * mm});
            skLineSegment(sketch, "E32.0.12.0", {"start": v(3057.52, 2294.6) * mm, "end": v(3327.4, 2294.6) * mm});
            skLineSegment(sketch, "E32.3.12.0", {"start": v(3073.4, 2269.2) * mm, "end": v(3327.4, 2269.2) * mm});
            skPoint(sketch, "E32.6.12.0", {"position": v(3065.46, 2269.2) * mm});
            skPoint(sketch, "E32.7.12.0", {"position": v(3050.79, 2271.99) * mm});
            skLineSegment(sketch, "E32.8.12.0", {"start": v(3327.4, 2294.6) * mm, "end": v(3327.4, 2269.2) * mm});
            skArc(sketch, "E32.11.12.0", {"start": v(3048, 2278.72) * mm, "mid": v(3050.79, 2271.99) * mm, "end": v(3057.52, 2269.2) * mm});
            skLineSegment(sketch, "E32.15.12.0", {"start": v(3057.52, 2269.2) * mm, "end": v(3073.4, 2269.2) * mm});
            skLineSegment(sketch, "E32.18.12.0", {"start": v(3048, 2278.72) * mm, "end": v(3048, 2285.07) * mm});
            skArc(sketch, "E32.21.12.0", {"start": v(3057.52, 2294.6) * mm, "mid": v(3050.79, 2291.81) * mm, "end": v(3048, 2285.07) * mm});
            skLineSegment(sketch, "E32.0.13.0", {"start": v(3311.52, 2483.7) * mm, "end": v(3581.4, 2483.7) * mm});
            skLineSegment(sketch, "E32.3.13.0", {"start": v(3327.4, 2458.3) * mm, "end": v(3581.4, 2458.3) * mm});
            skPoint(sketch, "E32.6.13.0", {"position": v(3319.46, 2458.3) * mm});
            skPoint(sketch, "E32.7.13.0", {"position": v(3304.79, 2461.09) * mm});
            skLineSegment(sketch, "E32.8.13.0", {"start": v(3581.4, 2483.7) * mm, "end": v(3581.4, 2458.3) * mm});
            skArc(sketch, "E32.11.13.0", {"start": v(3302, 2467.83) * mm, "mid": v(3304.79, 2461.09) * mm, "end": v(3311.52, 2458.3) * mm});
            skLineSegment(sketch, "E32.15.13.0", {"start": v(3311.52, 2458.3) * mm, "end": v(3327.4, 2458.3) * mm});
            skLineSegment(sketch, "E32.18.13.0", {"start": v(3302, 2467.83) * mm, "end": v(3302, 2474.18) * mm});
            skArc(sketch, "E32.21.13.0", {"start": v(3311.52, 2483.7) * mm, "mid": v(3304.79, 2480.91) * mm, "end": v(3302, 2474.18) * mm});
            skLineSegment(sketch, "E32.0.14.0", {"start": v(3565.52, 2672.8) * mm, "end": v(3835.4, 2672.8) * mm});
            skLineSegment(sketch, "E32.3.14.0", {"start": v(3581.4, 2647.4) * mm, "end": v(3835.4, 2647.4) * mm});
            skPoint(sketch, "E32.6.14.0", {"position": v(3573.46, 2647.4) * mm});
            skPoint(sketch, "E32.7.14.0", {"position": v(3558.79, 2650.19) * mm});
            skLineSegment(sketch, "E32.8.14.0", {"start": v(3835.4, 2672.8) * mm, "end": v(3835.4, 2647.4) * mm});
            skArc(sketch, "E32.11.14.0", {"start": v(3556, 2656.93) * mm, "mid": v(3558.79, 2650.19) * mm, "end": v(3565.52, 2647.4) * mm});
            skLineSegment(sketch, "E32.15.14.0", {"start": v(3565.52, 2647.4) * mm, "end": v(3581.4, 2647.4) * mm});
            skLineSegment(sketch, "E32.18.14.0", {"start": v(3556, 2656.93) * mm, "end": v(3556, 2663.28) * mm});
            skArc(sketch, "E32.21.14.0", {"start": v(3565.52, 2672.8) * mm, "mid": v(3558.79, 2670.01) * mm, "end": v(3556, 2663.28) * mm});
            skLineSegment(sketch, "E33", {"start": v(279.4, 0) * mm, "end": v(533.4, 189.1) * mm, "construction": true});
            skSolve(sketch);
        }
        {
            var Q0;
            Q0=qSketchRegion(id+"F2",true);
            extrude(context, id + "F3", {"entities" : qUnion([Q0]), "operationType" : NewBodyOperationType.ADD, "depth" : 25.4 * mm, "offsetDistance" : 25.4 * mm});
        }
        {
            var Q0;
            Q0=makeQuery(id+"F1.opExtrude","SWEPT_FACE",FACE,{"disambiguationData":[OSD([sQuery(id+"F0.wireOp",EDGE,"E9")])]});
            var sketch = newSketch(context, id + "F4", { "sketchPlane" : qUnion([Q0])});
            skCircle(sketch, "E34.2.0.0", {"center": v(279.78, 1079.5) * mm, "radius": 6.35 * mm});
            skCircle(sketch, "E34.2.0.1", {"center": v(160.02, 1079.5) * mm, "radius": 6.35 * mm});
            skCircle(sketch, "E34.2.0.2", {"center": v(192.68, 1079.5) * mm, "radius": 6.35 * mm});
            skCircle(sketch, "E34.2.0.3", {"center": v(453.97, 1079.5) * mm, "radius": 6.35 * mm});
            skCircle(sketch, "E34.2.0.4", {"center": v(366.88, 1079.5) * mm, "radius": 6.35 * mm});
            skCircle(sketch, "E34.3.0.0", {"center": v(660.78, 1079.5) * mm, "radius": 6.35 * mm});
            skCircle(sketch, "E34.3.0.1", {"center": v(541.02, 1079.5) * mm, "radius": 6.35 * mm});
            skCircle(sketch, "E34.3.0.2", {"center": v(573.68, 1079.5) * mm, "radius": 6.35 * mm});
            skCircle(sketch, "E34.3.0.3", {"center": v(834.97, 1079.5) * mm, "radius": 6.35 * mm});
            skCircle(sketch, "E34.3.0.4", {"center": v(747.88, 1079.5) * mm, "radius": 6.35 * mm});
            skCircle(sketch, "E35.1.0.0", {"center": v(954.68, 1079.5) * mm, "radius": 6.35 * mm});
            skCircle(sketch, "E35.1.0.1", {"center": v(1509.88, 1079.5) * mm, "radius": 6.35 * mm});
            skCircle(sketch, "E35.1.0.2", {"center": v(1041.78, 1079.5) * mm, "radius": 6.35 * mm});
            skCircle(sketch, "E35.1.0.3", {"center": v(1215.97, 1079.5) * mm, "radius": 6.35 * mm});
            skCircle(sketch, "E35.1.0.4", {"center": v(1303.02, 1079.5) * mm, "radius": 6.35 * mm});
            skCircle(sketch, "E35.1.0.5", {"center": v(922.02, 1079.5) * mm, "radius": 6.35 * mm});
            skCircle(sketch, "E35.1.0.6", {"center": v(1422.78, 1079.5) * mm, "radius": 6.35 * mm});
            skCircle(sketch, "E35.1.0.7", {"center": v(1335.68, 1079.5) * mm, "radius": 6.35 * mm});
            skCircle(sketch, "E35.1.0.8", {"center": v(1596.97, 1079.5) * mm, "radius": 6.35 * mm});
            skCircle(sketch, "E35.1.0.9", {"center": v(1128.88, 1079.5) * mm, "radius": 6.35 * mm});
            skCircle(sketch, "E35.2.0.0", {"center": v(1716.68, 1079.5) * mm, "radius": 6.35 * mm});
            skCircle(sketch, "E35.2.0.1", {"center": v(2271.88, 1079.5) * mm, "radius": 6.35 * mm});
            skCircle(sketch, "E35.2.0.2", {"center": v(1803.78, 1079.5) * mm, "radius": 6.35 * mm});
            skCircle(sketch, "E35.2.0.3", {"center": v(1977.97, 1079.5) * mm, "radius": 6.35 * mm});
            skCircle(sketch, "E35.2.0.4", {"center": v(2065.02, 1079.5) * mm, "radius": 6.35 * mm});
            skCircle(sketch, "E35.2.0.5", {"center": v(1684.02, 1079.5) * mm, "radius": 6.35 * mm});
            skCircle(sketch, "E35.2.0.6", {"center": v(2184.78, 1079.5) * mm, "radius": 6.35 * mm});
            skCircle(sketch, "E35.2.0.7", {"center": v(2097.68, 1079.5) * mm, "radius": 6.35 * mm});
            skCircle(sketch, "E35.2.0.8", {"center": v(2358.97, 1079.5) * mm, "radius": 6.35 * mm});
            skCircle(sketch, "E35.2.0.9", {"center": v(1890.88, 1079.5) * mm, "radius": 6.35 * mm});
            skCircle(sketch, "E35.3.0.0", {"center": v(2478.68, 1079.5) * mm, "radius": 6.35 * mm});
            skCircle(sketch, "E35.3.0.1", {"center": v(3033.88, 1079.5) * mm, "radius": 6.35 * mm});
            skCircle(sketch, "E35.3.0.2", {"center": v(2565.78, 1079.5) * mm, "radius": 6.35 * mm});
            skCircle(sketch, "E35.3.0.3", {"center": v(2739.97, 1079.5) * mm, "radius": 6.35 * mm});
            skCircle(sketch, "E35.3.0.4", {"center": v(2827.02, 1079.5) * mm, "radius": 6.35 * mm});
            skCircle(sketch, "E35.3.0.5", {"center": v(2446.02, 1079.5) * mm, "radius": 6.35 * mm});
            skCircle(sketch, "E35.3.0.6", {"center": v(2946.78, 1079.5) * mm, "radius": 6.35 * mm});
            skCircle(sketch, "E35.3.0.7", {"center": v(2859.68, 1079.5) * mm, "radius": 6.35 * mm});
            skCircle(sketch, "E35.3.0.8", {"center": v(3120.97, 1079.5) * mm, "radius": 6.35 * mm});
            skCircle(sketch, "E35.3.0.9", {"center": v(2652.88, 1079.5) * mm, "radius": 6.35 * mm});
            skCircle(sketch, "E35.4.0.0", {"center": v(3240.68, 1079.5) * mm, "radius": 6.35 * mm});
            skCircle(sketch, "E35.4.0.1", {"center": v(3795.88, 1079.5) * mm, "radius": 6.35 * mm});
            skCircle(sketch, "E35.4.0.2", {"center": v(3327.78, 1079.5) * mm, "radius": 6.35 * mm});
            skCircle(sketch, "E35.4.0.3", {"center": v(3501.97, 1079.5) * mm, "radius": 6.35 * mm});
            skCircle(sketch, "E35.4.0.4", {"center": v(3589.02, 1079.5) * mm, "radius": 6.35 * mm});
            skCircle(sketch, "E35.4.0.5", {"center": v(3208.02, 1079.5) * mm, "radius": 6.35 * mm});
            skCircle(sketch, "E35.4.0.6", {"center": v(3708.78, 1079.5) * mm, "radius": 6.35 * mm});
            skCircle(sketch, "E35.4.0.7", {"center": v(3621.68, 1079.5) * mm, "radius": 6.35 * mm});
            skCircle(sketch, "E35.4.0.8", {"center": v(3882.97, 1079.5) * mm, "radius": 6.35 * mm});
            skCircle(sketch, "E35.4.0.9", {"center": v(3414.88, 1079.5) * mm, "radius": 6.35 * mm});
            skLineSegment(sketch, "E35.direction1", {"start": v(160.02, 1079.5) * mm, "end": v(922.02, 1079.5) * mm, "construction": true});
            skSolve(sketch);
        }
        {
            var Q0;
            Q0=qSketchRegion(id+"F4",true);
            extrude(context, id + "F5", {"entities" : qUnion([Q0]), "operationType" : NewBodyOperationType.REMOVE, "endBound" : BoundingType.THROUGH_ALL, "oppositeDirection" : true, "depth" : 25.4 * mm, "offsetDistance" : 25.4 * mm});
        }
        {
            var Q0;
            Q0=makeQuery(id+"F3.boolean.opBoolean","MERGE",FACE,{"derivedFrom":[makeQuery(id+"F1.opExtrude","SWEPT_FACE",FACE,{"disambiguationData":[OSD([sQuery(id+"F0.wireOp",EDGE,"E0.top")])]}),makeQuery(id+"F3.opExtrude","SWEPT_FACE",FACE,{"disambiguationData":[OSD([sQuery(id+"F2.wireOp",EDGE,"E28.4")])]})]});
            var sketch = newSketch(context, id + "F6", { "sketchPlane" : qUnion([Q0])});
            skLineSegment(sketch, "E36.bottom", {"start": v(166.37, -1085.85) * mm, "end": v(153.67, -1085.85) * mm});
            skLineSegment(sketch, "E36.top", {"start": v(166.37, -1073.15) * mm, "end": v(153.67, -1073.15) * mm});
            skLineSegment(sketch, "E36.left", {"start": v(166.37, -1085.85) * mm, "end": v(166.37, -1073.15) * mm});
            skLineSegment(sketch, "E36.right", {"start": v(153.67, -1085.85) * mm, "end": v(153.67, -1073.15) * mm});
            skPoint(sketch, "E36.middle", {"position": v(160.02, -1079.5) * mm});
            skSolve(sketch);
        }
        {
            var Q0;
            Q0 = qSketchRegion(id + "F6", true);
            extrude(context, id + "F7", {"entities" : qUnion([Q0]), "operationType" : NewBodyOperationType.REMOVE, "oppositeDirection" : true, "depth" : 19.05 * mm, "offsetDistance" : 25.4 * mm});
        }
        {
            var Q0;
            Q0=makeQuery(id+"F3.boolean.opBoolean","MERGE",FACE,{"derivedFrom":[makeQuery(id+"F1.opExtrude","SWEPT_FACE",FACE,{"disambiguationData":[OSD([sQuery(id+"F0.wireOp",EDGE,"E0.top")])]}),makeQuery(id+"F3.opExtrude","SWEPT_FACE",FACE,{"disambiguationData":[OSD([sQuery(id+"F2.wireOp",EDGE,"E28.4")])]})]});
            var sketch = newSketch(context, id + "F8", { "sketchPlane" : qUnion([Q0])});
            skLineSegment(sketch, "E37.bottom", {"start": v(95.7, -1028.7) * mm, "end": v(-5.9, -1028.7) * mm});
            skLineSegment(sketch, "E37.top", {"start": v(95.7, -1130.3) * mm, "end": v(-5.9, -1130.3) * mm});
            skLineSegment(sketch, "E37.left", {"start": v(95.7, -1028.7) * mm, "end": v(95.7, -1130.3) * mm});
            skLineSegment(sketch, "E37.right", {"start": v(-5.9, -1028.7) * mm, "end": v(-5.9, -1130.3) * mm});
            skSolve(sketch);
        }
        {
            var Q0;
            Q0 = qSketchRegion(id + "F8", true);
            extrude(context, id + "F9", {"entities" : qUnion([Q0]), "operationType" : NewBodyOperationType.ADD, "depth" : 1028.7 * mm, "offsetDistance" : 25.4 * mm});
        }
        {
            var Q0;
            Q0=makeQuery(id+"F1.opExtrude","SWEPT_FACE",FACE,{"disambiguationData":[OSD([sQuery(id+"F0.wireOp",EDGE,"E11")])]});
            var sketch = newSketch(context, id + "F10", { "sketchPlane" : qUnion([Q0])});
            skLineSegment(sketch, "E38.bottom", {"start": v(3905.25, -1028.7) * mm, "end": v(3803.65, -1028.7) * mm});
            skLineSegment(sketch, "E38.top", {"start": v(3905.25, -1130.3) * mm, "end": v(3803.65, -1130.3) * mm});
            skLineSegment(sketch, "E38.left", {"start": v(3905.25, -1028.7) * mm, "end": v(3905.25, -1130.3) * mm});
            skLineSegment(sketch, "E38.right", {"start": v(3803.65, -1028.7) * mm, "end": v(3803.65, -1130.3) * mm});
            skSolve(sketch);
        }
        {
            var Q0;
            Q0 = qSketchRegion(id + "F10", true);
            extrude(context, id + "F11", {"entities" : qUnion([Q0]), "operationType" : NewBodyOperationType.ADD, "depth" : 938 * mm, "offsetDistance" : 25.4 * mm});
        }
        {
            var Q0;
            Q0=makeQuery(id+"F9.opExtrude","SWEPT_FACE",FACE,{"disambiguationData":[OSD([sQuery(id+"F8.wireOp",EDGE,"E37.left")])]});
            var sketch = newSketch(context, id + "F12", { "sketchPlane" : qUnion([Q0])});
            skCircle(sketch, "E39", {"center": v(-1078.7, 968.4) * mm, "radius": 3 * mm});
            skSolve(sketch);
        }
        {
            var Q0;
            Q0 = qSketchRegion(id + "F12", true);
            extrude(context, id + "F13", {"entities" : qUnion([Q0]), "operationType" : NewBodyOperationType.REMOVE, "oppositeDirection" : true, "depth" : 25 * mm, "offsetDistance" : 25 * mm});
        }
    });
